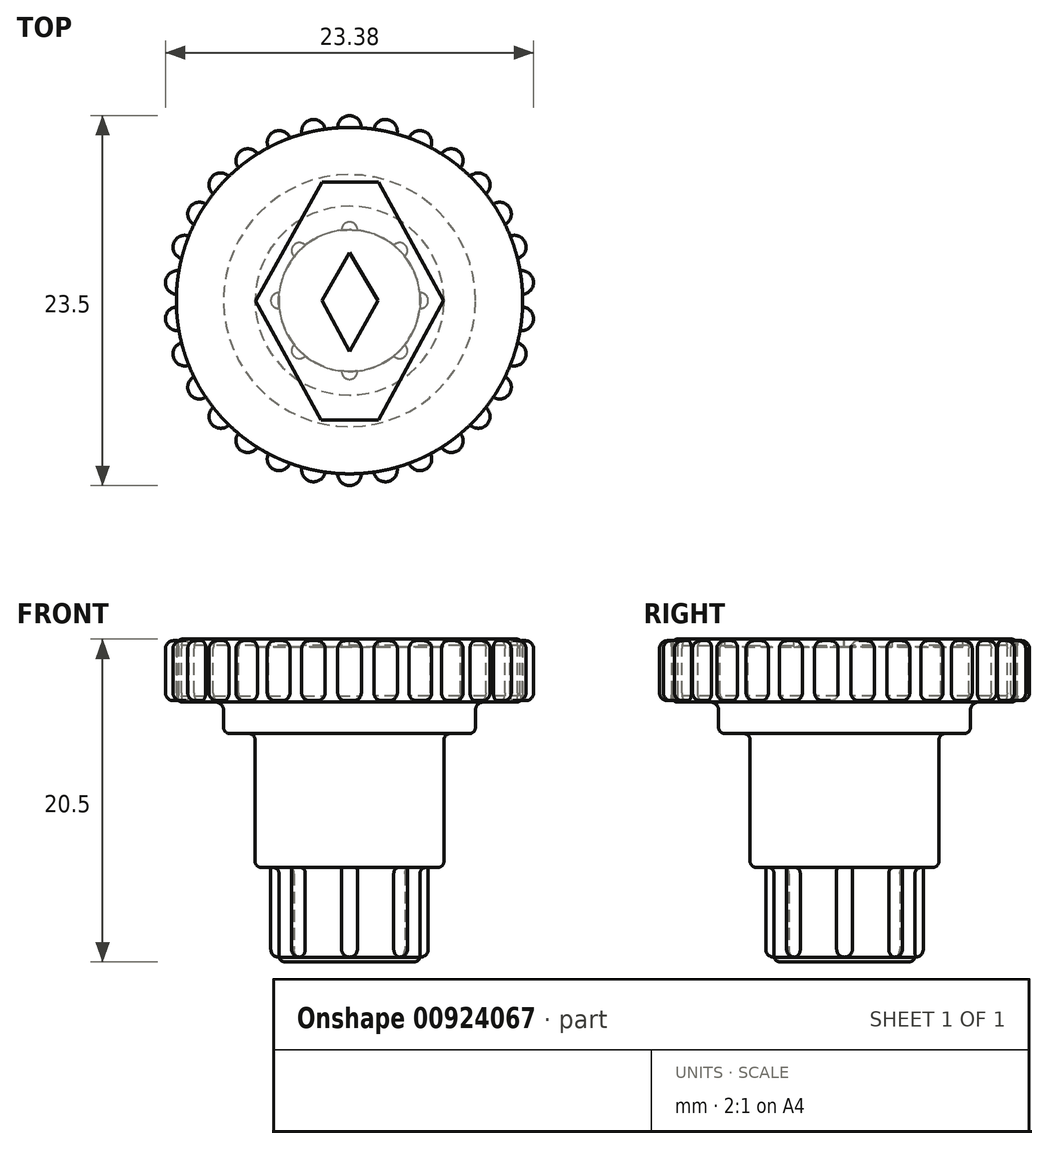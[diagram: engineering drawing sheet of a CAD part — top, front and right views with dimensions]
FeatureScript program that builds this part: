
annotation { "Feature Type Name" : "Feature", "Feature Type Description" : "" }
export const myFeature = defineFeature(function(context is Context, id is Id, definition is map)
    precondition{}
    {
        {
            var Q0;
            Q0=qCreatedBy(makeId("Front.planeOp"),FACE);
            var sketch = newSketch(context, id + "F0", { "sketchPlane" : qUnion([Q0])});
            skLineSegment(sketch, "E0", {"start": v(0, 0) * mm, "end": v(0, 20.5) * mm});
            skLineSegment(sketch, "E1", {"start": v(0, 20.5) * mm, "end": v(11, 20.5) * mm});
            skLineSegment(sketch, "E2", {"start": v(11, 20.5) * mm, "end": v(11, 16.5) * mm});
            skLineSegment(sketch, "E3", {"start": v(11, 16.5) * mm, "end": v(8, 16.5) * mm});
            skLineSegment(sketch, "E4", {"start": v(8, 16.5) * mm, "end": v(8, 14.5) * mm});
            skLineSegment(sketch, "E5", {"start": v(8, 14.5) * mm, "end": v(6, 14.5) * mm});
            skLineSegment(sketch, "E6", {"start": v(6, 14.5) * mm, "end": v(6, 6) * mm});
            skLineSegment(sketch, "E7", {"start": v(6, 6) * mm, "end": v(4.5, 6) * mm});
            skLineSegment(sketch, "E8", {"start": v(4.5, 6) * mm, "end": v(4.5, 0) * mm});
            skLineSegment(sketch, "E9", {"start": v(4.5, 0) * mm, "end": v(0, 0) * mm});
            skSolve(sketch);
        }
        {
            var Q0;
            Q0=makeQuery(id+"F0.imprint","IMPRINT",FACE,{"disambiguationData":[TD([[makeQuery(id+"F0.imprint","IMPRINT",EDGE,{"derivedFrom":sQuery(id+"F0.wireOp",EDGE,"E0")}),-1.0]])]});
            var Q1;
            Q1=sQuery(id+"F0.wireOp",EDGE,"E0");
            revolve(context, id + "F1", {"surfaceOperationType" : NewSurfaceOperationType.NEW, "entities" : qUnion([Q0]), "axis" : qUnion([Q1]), "revolveType" : RevolveType.FULL});
        }
        {
            var Q0;
            Q0=makeQuery(id+"F1.opRevolve","SWEPT_EDGE",EDGE,{"disambiguationData":[OSD([sQuery(id+"F0.wireOp",EDGE,"E3"),sQuery(id+"F0.wireOp",EDGE,"E4")])]});
            fillet(context, id + "F2", {"entities" : qUnion([Q0]), "radius" : 0.5 * mm, "tangentPropagation" : true, "allowEdgeOverflow" : false});
        }
        {
            var Q0;
            Q0=makeQuery(id+"F1.opRevolve","SWEPT_EDGE",EDGE,{"disambiguationData":[OSD([sQuery(id+"F0.wireOp",EDGE,"E2"),sQuery(id+"F0.wireOp",EDGE,"E3")])]});
            var Q1;
            Q1=makeQuery(id+"F1.opRevolve","SWEPT_EDGE",EDGE,{"disambiguationData":[OSD([sQuery(id+"F0.wireOp",EDGE,"E1"),sQuery(id+"F0.wireOp",EDGE,"E2")])]});
            fillet(context, id + "F3", {"entities" : qUnion([Q0, Q1]), "radius" : 0.4 * mm, "tangentPropagation" : true, "allowEdgeOverflow" : false});
        }
        {
            var Q0;
            Q0=makeQuery(id+"F1.opRevolve","SWEPT_FACE",FACE,{"disambiguationData":[OSD([sQuery(id+"F0.wireOp",EDGE,"E1")])]});
            cPlane(context, id + "F4", {"entities" : qUnion([Q0]), "cplaneType" : CPlaneType.OFFSET, "offset" : 0 * mm, "width" : 150 * mm, "height" : 150 * mm});
        }
        {
            var Q0;
            Q0=qCreatedBy(id+"F4.planeOp",FACE);
            var sketch = newSketch(context, id + "F5", { "sketchPlane" : qUnion([Q0])});
            skCircle(sketch, "E10", {"center": v(0, 0) * mm, "radius": 11 * mm});
            skArc(sketch, "E11", {"start": v(-0.75, -10.97) * mm, "mid": v(0, -11.75) * mm, "end": v(0.75, -10.97) * mm});
            skSolve(sketch);
        }
        {
            var Q0;
            {var subQ0=sQuery(id+"F5.wireOp",EDGE,"E11");Q0=makeQuery(id+"F5.imprint","IMPRINT",FACE,{"disambiguationData":[TD([[makeQuery(id+"F5.imprint","IMPRINT",EDGE,{"derivedFrom":subQ0}),1.0]])]});}
            extrude(context, id + "F6", {"entities" : qUnion([Q0]), "operationType" : NewBodyOperationType.ADD, "oppositeDirection" : true, "depth" : 3.91 * mm, "offsetDistance" : 25 * mm, "hasSecondDirection" : true, "secondDirectionOppositeDirection" : true, "secondDirectionDepth" : 0.1 * mm});
        }
        {
            var Q0;
            Q0=makeQuery(id+"F6.opExtrude","CAP_EDGE",EDGE,{"disambiguationData":[OSD([sQuery(id+"F5.wireOp",EDGE,"E11")])],"isStart":true});
            var Q1;
            Q1=makeQuery(id+"F6.opExtrude","CAP_EDGE",EDGE,{"disambiguationData":[OSD([sQuery(id+"F5.wireOp",EDGE,"E11")])],"isStart":false});
            fillet(context, id + "F7", {"entities" : qUnion([Q0, Q1]), "radius" : 0.5 * mm, "tangentPropagation" : true, "allowEdgeOverflow" : false});
        }
        {
            var Q0;
            Q0=makeQuery(id+"F1.opRevolve","SWEPT_BODY",BODY,{"disambiguationData":[OSD([sQuery(id+"F0.wireOp",EDGE,"E0"),sQuery(id+"F0.wireOp",EDGE,"E1"),sQuery(id+"F0.wireOp",EDGE,"E2"),sQuery(id+"F0.wireOp",EDGE,"E3"),sQuery(id+"F0.wireOp",EDGE,"E4"),sQuery(id+"F0.wireOp",EDGE,"E5"),sQuery(id+"F0.wireOp",EDGE,"E6"),sQuery(id+"F0.wireOp",EDGE,"E7"),sQuery(id+"F0.wireOp",EDGE,"E8"),sQuery(id+"F0.wireOp",EDGE,"E9")])]});
            var Q1;
            Q1=makeQuery(id+"F1.opRevolve","SWEPT_FACE",FACE,{"disambiguationData":[OSD([sQuery(id+"F0.wireOp",EDGE,"E2")])]});
            circularPattern(context, id + "F8", {"operationType" : NewBodyOperationType.ADD, "entities" : qUnion([Q0]), "axis" : qUnion([Q1]), "angle" : 360 * degree, "instanceCount" : 30, "equalSpace" : true, "computeTransformsWithoutBuiltin" : true});
        }
        {
            var Q0;
            Q0=qCreatedBy(id+"F4.planeOp",FACE);
            var sketch = newSketch(context, id + "F9", { "sketchPlane" : qUnion([Q0])});
            skLineSegment(sketch, "E12", {"start": v(-1.73, 7.52) * mm, "end": v(1.86, 7.52) * mm});
            skLineSegment(sketch, "E13", {"start": v(1.86, 7.52) * mm, "end": v(5.96, 0) * mm});
            skLineSegment(sketch, "E14", {"start": v(5.96, 0) * mm, "end": v(1.83, -7.58) * mm});
            skLineSegment(sketch, "E15", {"start": v(1.83, -7.58) * mm, "end": v(-1.82, -7.58) * mm});
            skLineSegment(sketch, "E16", {"start": v(-1.82, -7.58) * mm, "end": v(-5.97, -0.03) * mm});
            skLineSegment(sketch, "E17", {"start": v(-5.97, -0.03) * mm, "end": v(-1.73, 7.52) * mm});
            skLineSegment(sketch, "E18", {"start": v(0, 3.05) * mm, "end": v(-1.73, 0) * mm});
            skLineSegment(sketch, "E19", {"start": v(-1.73, 0) * mm, "end": v(0, -3.23) * mm});
            skLineSegment(sketch, "E20", {"start": v(0, -3.23) * mm, "end": v(1.8, 0) * mm});
            skLineSegment(sketch, "E21", {"start": v(1.8, 0) * mm, "end": v(0, 3.05) * mm});
            skSolve(sketch);
        }
        {
            var Q0;
            Q0=makeQuery(id+"F9.imprint","IMPRINT",FACE,{"disambiguationData":[TD([[makeQuery(id+"F9.imprint","IMPRINT",EDGE,{"derivedFrom":sQuery(id+"F9.wireOp",EDGE,"E12")}),-1.0]])]});
            extrude(context, id + "F10", {"entities" : qUnion([Q0]), "operationType" : NewBodyOperationType.REMOVE, "oppositeDirection" : true, "depth" : 0.5 * mm, "offsetDistance" : 25 * mm});
        }
        {
            var Q0;
            Q0=makeQuery(id+"F1.opRevolve","SWEPT_EDGE",EDGE,{"disambiguationData":[OSD([sQuery(id+"F0.wireOp",EDGE,"E6"),sQuery(id+"F0.wireOp",EDGE,"E7")])]});
            var Q1;
            Q1=makeQuery(id+"F1.opRevolve","SWEPT_EDGE",EDGE,{"disambiguationData":[OSD([sQuery(id+"F0.wireOp",EDGE,"E7"),sQuery(id+"F0.wireOp",EDGE,"E8")])]});
            var Q2;
            Q2=makeQuery(id+"F1.opRevolve","SWEPT_EDGE",EDGE,{"disambiguationData":[OSD([sQuery(id+"F0.wireOp",EDGE,"E5"),sQuery(id+"F0.wireOp",EDGE,"E6")])]});
            var Q3;
            Q3=makeQuery(id+"F1.opRevolve","SWEPT_EDGE",EDGE,{"disambiguationData":[OSD([sQuery(id+"F0.wireOp",EDGE,"E4"),sQuery(id+"F0.wireOp",EDGE,"E5")])]});
            var Q4;
            Q4=makeQuery(id+"F1.opRevolve","SWEPT_EDGE",EDGE,{"disambiguationData":[OSD([sQuery(id+"F0.wireOp",EDGE,"E8"),sQuery(id+"F0.wireOp",EDGE,"E9")])]});
            fillet(context, id + "F11", {"entities" : qUnion([Q0, Q1, Q2, Q3, Q4]), "radius" : 0.4 * mm, "tangentPropagation" : true, "allowEdgeOverflow" : false});
        }
        {
            var Q0;
            Q0=makeQuery(id+"F1.opRevolve","SWEPT_FACE",FACE,{"disambiguationData":[OSD([sQuery(id+"F0.wireOp",EDGE,"E9")])]});
            cPlane(context, id + "F12", {"entities" : qUnion([Q0]), "cplaneType" : CPlaneType.OFFSET, "offset" : 0.3 * mm, "oppositeDirection" : true, "width" : 150 * mm, "height" : 150 * mm});
        }
        {
            var Q0;
            Q0=qCreatedBy(id+"F12.planeOp",FACE);
            var sketch = newSketch(context, id + "F13", { "sketchPlane" : qUnion([Q0])});
            skArc(sketch, "E22", {"start": v(-0.5, 4.47) * mm, "mid": v(0, -4.5) * mm, "end": v(0.5, 4.47) * mm});
            skArc(sketch, "E23", {"start": v(0.5, 4.47) * mm, "mid": v(0, 5) * mm, "end": v(-0.5, 4.47) * mm});
            skArc(sketch, "E24.1.0", {"start": v(-2.8, 3.52) * mm, "mid": v(-3.54, 3.54) * mm, "end": v(-3.52, 2.8) * mm});
            skArc(sketch, "E24.2.0", {"start": v(-4.47, 0.5) * mm, "mid": v(-5, 0) * mm, "end": v(-4.47, -0.5) * mm});
            skArc(sketch, "E24.3.0", {"start": v(-3.52, -2.8) * mm, "mid": v(-3.54, -3.54) * mm, "end": v(-2.8, -3.52) * mm});
            skArc(sketch, "E24.4.0", {"start": v(-0.5, -4.47) * mm, "mid": v(0, -5) * mm, "end": v(0.5, -4.47) * mm});
            skArc(sketch, "E24.5.0", {"start": v(2.8, -3.52) * mm, "mid": v(3.54, -3.54) * mm, "end": v(3.52, -2.8) * mm});
            skArc(sketch, "E24.6.0", {"start": v(4.47, -0.5) * mm, "mid": v(5, 0) * mm, "end": v(4.47, 0.5) * mm});
            skArc(sketch, "E24.7.0", {"start": v(3.52, 2.8) * mm, "mid": v(3.54, 3.54) * mm, "end": v(2.8, 3.52) * mm});
            skSolve(sketch);
        }
        {
            var Q0;
            Q0 = qSketchRegion(id + "F13", true);
            extrude(context, id + "F14", {"entities" : qUnion([Q0]), "operationType" : NewBodyOperationType.ADD, "oppositeDirection" : true, "depth" : 7 * mm, "offsetDistance" : 25 * mm});
        }
        {
            var Q0;
            Q0=makeQuery(id+"F14.opExtrude","CAP_EDGE",EDGE,{"disambiguationData":[OSD([sQuery(id+"F13.wireOp",EDGE,"E24.7.0")])],"isStart":true});
            var Q1;
            Q1=makeQuery(id+"F14.opExtrude","CAP_EDGE",EDGE,{"disambiguationData":[OSD([sQuery(id+"F13.wireOp",EDGE,"E24.6.0")])],"isStart":true});
            var Q2;
            Q2=makeQuery(id+"F14.opExtrude","CAP_EDGE",EDGE,{"disambiguationData":[OSD([sQuery(id+"F13.wireOp",EDGE,"E24.5.0")])],"isStart":true});
            var Q3;
            Q3=makeQuery(id+"F14.opExtrude","CAP_EDGE",EDGE,{"disambiguationData":[OSD([sQuery(id+"F13.wireOp",EDGE,"E23")])],"isStart":true});
            var Q4;
            Q4=makeQuery(id+"F14.opExtrude","CAP_EDGE",EDGE,{"disambiguationData":[OSD([sQuery(id+"F13.wireOp",EDGE,"E24.1.0")])],"isStart":true});
            var Q5;
            Q5=makeQuery(id+"F14.opExtrude","CAP_EDGE",EDGE,{"disambiguationData":[OSD([sQuery(id+"F13.wireOp",EDGE,"E24.4.0")])],"isStart":true});
            var Q6;
            Q6=makeQuery(id+"F14.opExtrude","CAP_EDGE",EDGE,{"disambiguationData":[OSD([sQuery(id+"F13.wireOp",EDGE,"E24.3.0")])],"isStart":true});
            var Q7;
            Q7=makeQuery(id+"F14.opExtrude","CAP_EDGE",EDGE,{"disambiguationData":[OSD([sQuery(id+"F13.wireOp",EDGE,"E24.2.0")])],"isStart":true});
            fillet(context, id + "F15", {"entities" : qUnion([Q0, Q1, Q2, Q3, Q4, Q5, Q6, Q7]), "radius" : 0.5 * mm, "tangentPropagation" : true, "allowEdgeOverflow" : false});
        }
    });
